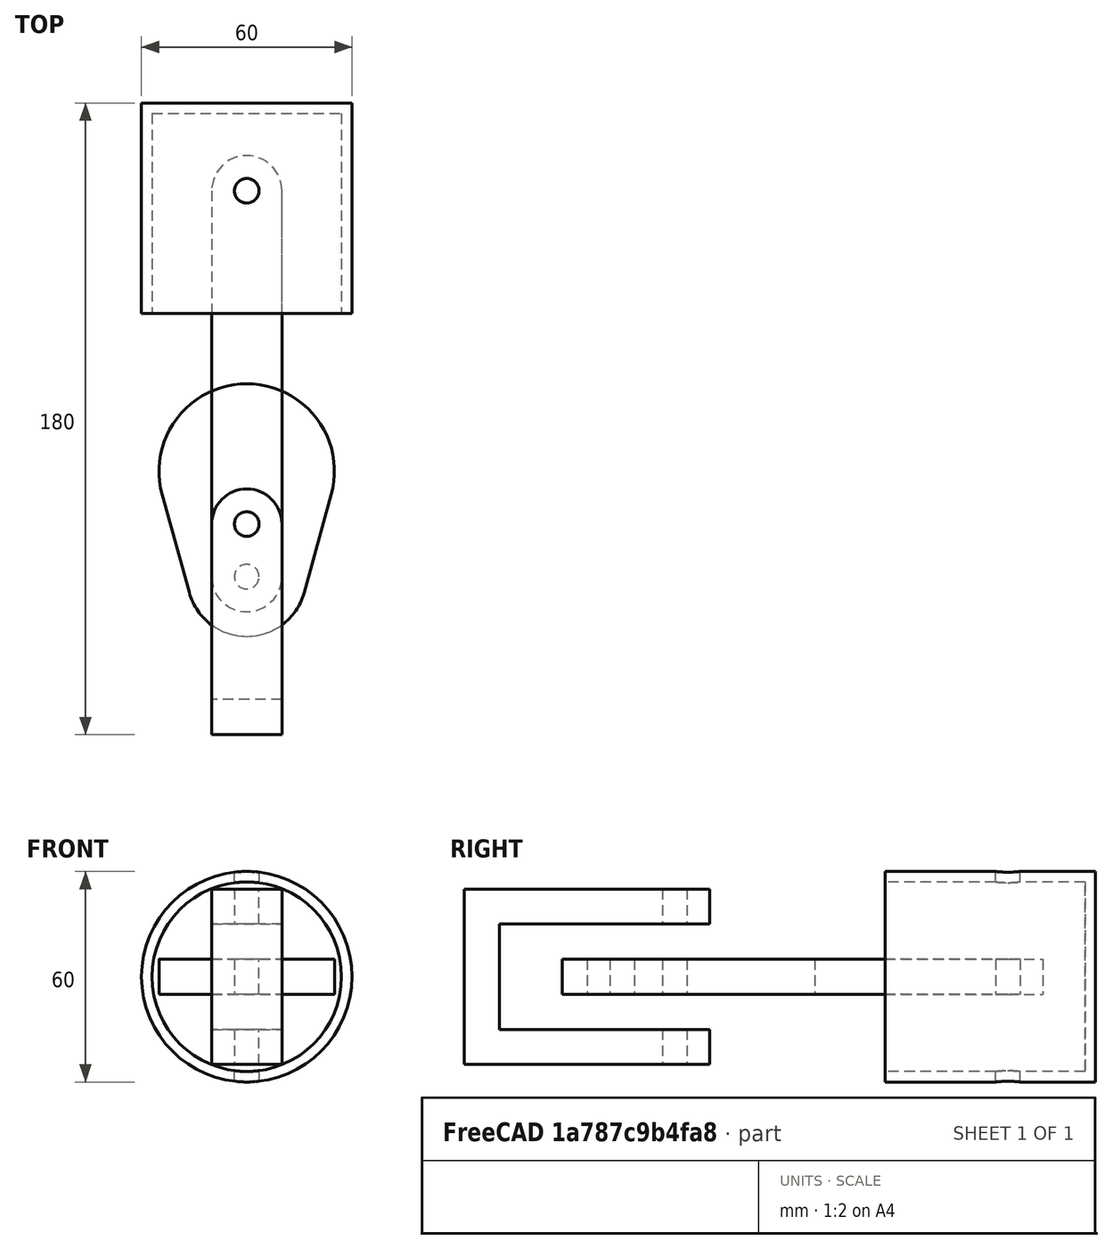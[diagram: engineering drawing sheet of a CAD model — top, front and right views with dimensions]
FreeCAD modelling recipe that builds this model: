
FCSTD DOCUMENT  (FreeCAD 1.0R39319 (Git))
Label: Piston Head Assembly
License: All rights reserved
LicenseURL: https://en.wikipedia.org/wiki/All_rights_reserved
objects: Sketcher::SketchObject×7, App::FeaturePython×6, App::Link×5, PartDesign::SubShapeBinder×4, PartDesign::Body×4, PartDesign::Pad×3, PartDesign::Pocket×2, PartDesign::Revolution×1, Assembly::JointGroup×1, Assembly::AssemblyObject×1
note: 40 computed .brp shape members not serialized (recipe doc carries the construction recipe); baked Part::Feature solids carry a one-line shape summary decoded from their .brp

FEATURE [Sketcher::SketchObject] Sketch  label="main_sketch"
  ArcFitTolerance = 1e-06
  AttachmentSupport = -> [XY_Plane]
  FullyConstrained = true
  MakeInternals = false
  MapMode = 5
  sketch-geometry (19):
    g0: ArcOfCircle CenterX=0 CenterY=55 CenterZ=0 NormalX=0 NormalY=0 NormalZ=1 AngleXU=0 Radius=10 StartAngle=3e-16 EndAngle=3.14159
    g1: ArcOfCircle CenterX=0 CenterY=-55 CenterZ=0 NormalX=0 NormalY=0 NormalZ=1 AngleXU=0 Radius=10 StartAngle=3.14159 EndAngle=6.28319
    g2: LineSegment StartX=10 StartY=55 StartZ=0 EndX=10 EndY=-55 EndZ=0
    g3: LineSegment StartX=-10 StartY=55 StartZ=0 EndX=-10 EndY=-55 EndZ=0
    g4: Circle CenterX=0 CenterY=55 CenterZ=0 NormalX=0 NormalY=0 NormalZ=1 AngleXU=0 Radius=3.5
    g5: Circle CenterX=0 CenterY=-55 CenterZ=0 NormalX=0 NormalY=0 NormalZ=1 AngleXU=0 Radius=3.5
    g6: ArcOfCircle CenterX=0 CenterY=-25 CenterZ=0 NormalX=0 NormalY=0 NormalZ=1 AngleXU=0 Radius=25 StartAngle=6.01325 EndAngle=9.69471
    g7: ArcOfCircle CenterX=0 CenterY=-55 CenterZ=0 NormalX=0 NormalY=0 NormalZ=1 AngleXU=0 Radius=17 StartAngle=3.41153 EndAngle=6.01325
    g8: LineSegment StartX=-24.0947 StartY=-31.6667 StartZ=0 EndX=-16.3844 EndY=-59.5333 EndZ=0
    g9: LineSegment StartX=16.3844 StartY=-59.5333 StartZ=0 EndX=24.0947 EndY=-31.6667 EndZ=0
    g10: Circle CenterX=8e-16 CenterY=-40 CenterZ=0 NormalX=0 NormalY=0 NormalZ=1 AngleXU=0 Radius=3.5
    g11: ArcOfCircle CenterX=8e-16 CenterY=-40 CenterZ=0 NormalX=0 NormalY=0 NormalZ=1 AngleXU=0 Radius=10 StartAngle=0 EndAngle=3.14159
    g12: LineSegment StartX=-30 StartY=80 StartZ=0 EndX=-30 EndY=20 EndZ=0
    g13: LineSegment StartX=-30 StartY=20 StartZ=0 EndX=30 EndY=20 EndZ=0
    g14: LineSegment StartX=30 StartY=20 StartZ=0 EndX=30 EndY=80 EndZ=0
    g15: LineSegment StartX=30 StartY=80 StartZ=0 EndX=-30 EndY=80 EndZ=0
    g16: LineSegment StartX=-10 StartY=-40 StartZ=0 EndX=-10 EndY=-100 EndZ=0
    g17: LineSegment StartX=10 StartY=-40 StartZ=0 EndX=10 EndY=-100 EndZ=0
    g18: LineSegment StartX=-10 StartY=-100 StartZ=0 EndX=10 EndY=-100 EndZ=0
  constraints (46):
    c: Tangent(g0,g2) = 1.5708
    c: Tangent(g0,g3) = -1.5708
    c: Tangent(g1,g2) = 1.5708
    c: Tangent(g1,g3) = -1.5708
    c: Equal(g0,g1)
    c: PointOnObject(g0,g-2)
    c: Symmetric(g0,g1,g-1)
    c: Radius(g0) = 10
    c: DistanceY(g2,g2) = 110
    c: Diameter(g4) = 7
    c: Coincident(g4,g0)
    c: Diameter(g5) = 7
    c: Coincident(g5,g1)
    c: PointOnObject(g6,g-2)
    c: DistanceY(g1,g6) = 30
    c: Radius(g6) = 25
    c: Radius(g7) = 17
    c: Coincident(g7,g1)
    c: Tangent(g8,g7) = -1.5708
    c: Tangent(g9,g7) = -1.5708
    c: Tangent(g8,g6) = -1.5708
    c: Tangent(g9,g6) = -1.5708
    c: Coincident(g11,g10)
    c: DistanceY(g10,g6) = 15
    c: Tangent(g11,g3) = -1.5708
    c: Tangent(g11,g2) = 1.5708
    c: Equal(g5,g10)
    c: Coincident(g12,g13)
    c: Coincident(g13,g14)
    c: Coincident(g14,g15)
    c: Coincident(g15,g12)
    c: Vertical(g12)
    c: Vertical(g14)
    c: Horizontal(g13)
    c: Equal(g15,g12)
    c: DistanceY(g12,g12) = 60
    c: Distance(g-1,g13) = 20
    c: Symmetric(g12,g14,g-2)
    c: Coincident(g16,g11)
    c: Vertical(g16)
    c: Coincident(g17,g11)
    c: Vertical(g17)
    c: Coincident(g18,g16)
    c: Coincident(g18,g17)
    c: Horizontal(g18)
    c: DistanceY(g16,g16) = 60
FEATURE [PartDesign::SubShapeBinder] Binder
  BindCopyOnChange = 0
  BindMode = 0
  ClaimChildren = false
  Context = -> Body [Binder.]
  Fuse = false
  MakeFace = false
  OffsetFill = false
  OffsetIntersection = false
  OffsetJoinType = 0
  OffsetOpenResult = false
  PartialLoad = false
  Refine = true
  Relative = true
  Support = -> [Sketch]
  _Version = 2
FEATURE [Sketcher::SketchObject] Sketch001
  ArcFitTolerance = 1e-06
  AttachmentSupport = -> [XY_Plane]
  ExternalGeometry = -> [Binder]
  FullyConstrained = true
  MakeInternals = false
  MapMode = 5
  sketch-geometry (6):
    g0: LineSegment StartX=-10 StartY=55 StartZ=0 EndX=-10 EndY=-55 EndZ=0
    g1: ArcOfCircle CenterX=3e-16 CenterY=-55 CenterZ=0 NormalX=0 NormalY=0 NormalZ=1 AngleXU=0 Radius=10 StartAngle=3.14159 EndAngle=6.28319
    g2: LineSegment StartX=10 StartY=-55 StartZ=0 EndX=10 EndY=55 EndZ=0
    g3: ArcOfCircle CenterX=-4e-16 CenterY=55 CenterZ=0 NormalX=0 NormalY=0 NormalZ=1 AngleXU=0 Radius=10 StartAngle=0 EndAngle=3.14159
    g4: Circle CenterX=3e-16 CenterY=-55 CenterZ=0 NormalX=0 NormalY=0 NormalZ=1 AngleXU=0 Radius=3.5
    g5: Circle CenterX=-4e-16 CenterY=55 CenterZ=0 NormalX=0 NormalY=0 NormalZ=1 AngleXU=0 Radius=3.5
  constraints (12):
    c: Coincident(g-4,g0)
    c: Coincident(g0,g-6)
    c: Tangent(g0,g1) = -1.5708
    c: Coincident(g1,g-6)
    c: Coincident(g1,g2)
    c: Coincident(g2,g-5)
    c: Tangent(g2,g3) = -1.5708
    c: Coincident(g3,g0)
    c: Coincident(g4,g1)
    c: Equal(g4,g-7)
    c: Coincident(g5,g3)
    c: Equal(g5,g-8)
FEATURE [PartDesign::SubShapeBinder] Binder001
  BindCopyOnChange = 0
  BindMode = 0
  ClaimChildren = false
  Context = -> Body001 [Binder001.]
  Fuse = false
  MakeFace = false
  OffsetFill = false
  OffsetIntersection = false
  OffsetJoinType = 0
  OffsetOpenResult = false
  PartialLoad = false
  Refine = true
  Relative = true
  Support = -> [Sketch]
  _Version = 2
FEATURE [Sketcher::SketchObject] Sketch002
  ArcFitTolerance = 1e-06
  AttachmentSupport = -> [XY_Plane001]
  ExternalGeometry = -> [Binder001]
  FullyConstrained = true
  MakeInternals = false
  MapMode = 5
  sketch-geometry (6):
    g0: LineSegment StartX=-30 StartY=20 StartZ=0 EndX=-30 EndY=80 EndZ=0
    g1: LineSegment StartX=-30 StartY=80 StartZ=0 EndX=0 EndY=80 EndZ=0
    g2: LineSegment StartX=0 StartY=80 StartZ=0 EndX=0 EndY=77 EndZ=0
    g3: LineSegment StartX=0 StartY=77 StartZ=0 EndX=-27 EndY=77 EndZ=0
    g4: LineSegment StartX=-27 StartY=77 StartZ=0 EndX=-27 EndY=20 EndZ=0
    g5: LineSegment StartX=-27 StartY=20 StartZ=0 EndX=-30 EndY=20 EndZ=0
  constraints (15):
    c: Coincident(g-6,g0)
    c: Coincident(g0,g-4)
    c: Coincident(g0,g1)
    c: Symmetric(g-4,g-4,g1)
    c: Coincident(g1,g2)
    c: PointOnObject(g2,g-2)
    c: Coincident(g2,g3)
    c: Horizontal(g3)
    c: Coincident(g3,g4)
    c: PointOnObject(g4,g-6)
    c: Vertical(g4)
    c: Coincident(g4,g5)
    c: Coincident(g5,g0)
    c: DistanceX(g5,g5) = 3
    c: DistanceY(g2,g2) = 3
FEATURE [PartDesign::Pad] Pad
  Direction = (0,0,1)
  Length = 10
  Length2 = 10
  Midplane = true
  Profile = -> Sketch001
  ReferenceAxis = -> Sketch001 [N_Axis]
  Refine = true
  Suppressed = false
  Type = 0
FEATURE [PartDesign::Body] Body  label="Link"
  AllowCompound = false
  Group = -> [Binder,Sketch001,Pad]
  Origin = -> Origin
  Tip = -> Pad
FEATURE [PartDesign::Revolution] Revolution
  Angle = 360
  Angle2 = 60
  Axis = (0,1,0)
  Base = (0,0,0)
  Profile = -> Sketch002
  ReferenceAxis = -> Sketch002 [V_Axis]
  Refine = true
  Suppressed = false
  Type = 0
FEATURE [PartDesign::SubShapeBinder] Binder002
  BindCopyOnChange = 0
  BindMode = 0
  ClaimChildren = false
  Context = -> Body002 [Binder002.]
  Fuse = false
  MakeFace = false
  OffsetFill = false
  OffsetIntersection = false
  OffsetJoinType = 0
  OffsetOpenResult = false
  PartialLoad = false
  Refine = true
  Relative = true
  Support = -> [Sketch]
  _Version = 2
FEATURE [Sketcher::SketchObject] Sketch003
  ArcFitTolerance = 1e-06
  AttachmentSupport = -> [XY_Plane002]
  ExternalGeometry = -> [Binder002]
  FullyConstrained = true
  MakeInternals = false
  MapMode = 5
  sketch-geometry (6):
    g0: LineSegment StartX=-24.0947 StartY=-31.6667 StartZ=0 EndX=-16.3844 EndY=-59.5333 EndZ=0
    g1: ArcOfCircle CenterX=0 CenterY=-55 CenterZ=0 NormalX=0 NormalY=0 NormalZ=1 AngleXU=0 Radius=17 StartAngle=3.41153 EndAngle=6.01325
    g2: LineSegment StartX=16.3844 StartY=-59.5333 StartZ=0 EndX=24.0947 EndY=-31.6667 EndZ=0
    g3: ArcOfCircle CenterX=-1.6e-15 CenterY=-25 CenterZ=0 NormalX=0 NormalY=0 NormalZ=1 AngleXU=0 Radius=25 StartAngle=6.01325 EndAngle=9.69471
    g4: Circle CenterX=0 CenterY=-40 CenterZ=0 NormalX=0 NormalY=0 NormalZ=1 AngleXU=0 Radius=3.5
    g5: Circle CenterX=0 CenterY=-55 CenterZ=0 NormalX=0 NormalY=0 NormalZ=1 AngleXU=0 Radius=3.5
  constraints (12):
    c: Coincident(g-4,g0)
    c: Tangent(g0,g1) = -1.5708
    c: Coincident(g1,g-6)
    c: Coincident(g1,g2)
    c: Coincident(g2,g-6)
    c: Tangent(g2,g3) = -1.5708
    c: Coincident(g3,g0)
    c: Coincident(g0,g-5)
    c: Coincident(g4,g-7)
    c: Equal(g4,g-7)
    c: Coincident(g5,g1)
    c: Equal(g5,g-8)
FEATURE [PartDesign::Pad] Pad001
  Direction = (0,0,1)
  Length = 10
  Length2 = 10
  Midplane = true
  Profile = -> Sketch003
  ReferenceAxis = -> Sketch003 [N_Axis]
  Refine = true
  Suppressed = false
  Type = 0
FEATURE [PartDesign::Body] Body002  label="Crank"
  AllowCompound = false
  Group = -> [Binder002,Sketch003,Pad001]
  Origin = -> Origin002
  Tip = -> Pad001
FEATURE [Sketcher::SketchObject] Sketch004
  ArcFitTolerance = 1e-06
  AttachmentSupport = -> [XY_Plane001]
  ExternalGeometry = -> [Binder001]
  FullyConstrained = true
  MakeInternals = false
  MapMode = 5
  sketch-geometry (1):
    g0: Circle CenterX=0 CenterY=55 CenterZ=0 NormalX=0 NormalY=0 NormalZ=1 AngleXU=0 Radius=3.5
  constraints (2):
    c: Coincident(g0,g-3)
    c: Equal(g0,g-3)
FEATURE [PartDesign::Pocket] Pocket
  BaseFeature = -> Revolution
  Direction = (0,0,-1)
  Length = 5
  Length2 = 5
  Midplane = true
  Profile = -> Sketch004
  ReferenceAxis = -> Sketch004 [N_Axis]
  Refine = true
  Suppressed = false
  Type = 1
FEATURE [PartDesign::Body] Body001  label="Piston Head"
  AllowCompound = false
  Group = -> [Binder001,Sketch002,Revolution,Sketch004,Pocket]
  Origin = -> Origin001
  Tip = -> Pocket
FEATURE [PartDesign::SubShapeBinder] Binder003
  BindCopyOnChange = 0
  BindMode = 0
  ClaimChildren = false
  Context = -> Body003 [Binder003.]
  Fuse = false
  MakeFace = false
  OffsetFill = false
  OffsetIntersection = false
  OffsetJoinType = 0
  OffsetOpenResult = false
  PartialLoad = false
  Refine = true
  Relative = true
  Support = -> [Sketch]
  _Version = 2
FEATURE [Sketcher::SketchObject] Sketch005
  ArcFitTolerance = 1e-06
  AttachmentSupport = -> [XY_Plane003]
  ExternalGeometry = -> [Binder003]
  FullyConstrained = true
  MakeInternals = false
  MapMode = 5
  sketch-geometry (5):
    g0: LineSegment StartX=-10 StartY=-40 StartZ=0 EndX=-10 EndY=-100 EndZ=0
    g1: LineSegment StartX=-10 StartY=-100 StartZ=0 EndX=10 EndY=-100 EndZ=0
    g2: LineSegment StartX=10 StartY=-100 StartZ=0 EndX=10 EndY=-40 EndZ=0
    g3: ArcOfCircle CenterX=1.8e-15 CenterY=-40 CenterZ=0 NormalX=0 NormalY=0 NormalZ=1 AngleXU=0 Radius=10 StartAngle=1e-16 EndAngle=3.14159
    g4: Circle CenterX=1.8e-15 CenterY=-40 CenterZ=0 NormalX=0 NormalY=0 NormalZ=1 AngleXU=0 Radius=3.5
  constraints (10):
    c: Tangent(g-4,g0) = -1.5708
    c: Coincident(g0,g1)
    c: Coincident(g1,g-6)
    c: Horizontal(g1)
    c: Coincident(g1,g2)
    c: Coincident(g2,g-5)
    c: Tangent(g2,g3) = -1.5708
    c: Coincident(g3,g0)
    c: Coincident(g4,g3)
    c: Equal(g4,g-7)
FEATURE [PartDesign::Pad] Pad002
  Direction = (0,0,1)
  Length = 50
  Length2 = 10
  Midplane = true
  Profile = -> Sketch005
  ReferenceAxis = -> Sketch005 [N_Axis]
  Refine = true
  Suppressed = false
  Type = 0
FEATURE [Sketcher::SketchObject] Sketch006
  ArcFitTolerance = 1e-06
  AttachmentSupport = -> [YZ_Plane003]
  ExternalGeometry = -> [Pad002]
  FullyConstrained = false
  MakeInternals = false
  MapMode = 5
  Placement = pos=(0,0,0) rot=(0.57735,0.57735,0.57735;2.0944rad)
  sketch-geometry (4):
    g0: LineSegment StartX=-90 StartY=15 StartZ=0 EndX=-90 EndY=-15 EndZ=0
    g1: LineSegment StartX=-90 StartY=-15 StartZ=0 EndX=-12.8642 EndY=-15 EndZ=0
    g2: LineSegment StartX=-12.8642 StartY=-15 StartZ=0 EndX=-12.8642 EndY=15 EndZ=0
    g3: LineSegment StartX=-12.8642 StartY=15 StartZ=0 EndX=-90 EndY=15 EndZ=0
  constraints (10):
    c: Coincident(g0,g1)
    c: Coincident(g1,g2)
    c: Coincident(g2,g3)
    c: Coincident(g3,g0)
    c: Vertical(g2)
    c: Horizontal(g1)
    c: Horizontal(g3)
    c: Symmetric(g0,g0,g-1)
    c: Distance(g1,g3) = 30
    c: Distance(g-3,g0) = 10
FEATURE [PartDesign::Pocket] Pocket001
  BaseFeature = -> Pad002
  Direction = (-1,0,0)
  Length = 30
  Length2 = 5
  Midplane = true
  Profile = -> Sketch006
  ReferenceAxis = -> Sketch006 [N_Axis]
  Refine = true
  Suppressed = false
  Type = 0
FEATURE [PartDesign::Body] Body003  label="Mount"
  AllowCompound = false
  Group = -> [Sketch005,Binder003,Pad002,Sketch006,Pocket001]
  Origin = -> Origin003
  Tip = -> Pocket001
FEATURE [App::Link] Mount  label="Mount001"
  LinkedObject = -> Body003
FEATURE [App::FeaturePython] GroundedJoint  # Assembly grounded joint (typed FeaturePython)
  ObjectToGround = -> Mount
FEATURE [App::Link] Crank  label="Crank001"
  LinkPlacement = pos=(9.6435,-78.8201,10) rot=(0,0,1;3.38508rad)
  LinkedObject = -> Body002
  Placement = pos=(9.6435,-78.8201,10) rot=(0,0,1;3.38508rad)
FEATURE [App::Link] Crank001  label="Crank002"
  LinkPlacement = pos=(9.6435,-78.8201,-10) rot=(0,0,1;3.38508rad)
  LinkedObject = -> Body002
  Placement = pos=(9.6435,-78.8201,-10) rot=(0,0,1;3.38508rad)
FEATURE [App::Link] Link  label="Link001"
  LinkPlacement = pos=(-1.80816,29.5278,-3e-16) rot=(0,0,-1;0.032881rad)
  LinkedObject = -> Body
  Placement = pos=(-1.80816,29.5278,-3e-16) rot=(0,0,-1;0.032881rad)
FEATURE [App::FeaturePython] Joint  label="Revolute"  # Assembly joint (typed FeaturePython)
  Activated = true
  AngleMax = 0
  AngleMin = 0
  Detach1 = false
  Detach2 = false
  Distance = 0
  Distance2 = 0
  EnableAngleMax = false
  EnableAngleMin = false
  EnableLengthMax = false
  EnableLengthMin = false
  JointType = 1 (Revolute)
  LengthMax = 0
  LengthMin = 0
  Offset2 = pos=(0,0,10) rot=(0,0,1;0rad)
  Placement1 = pos=(1.8e-15,-40,15) rot=(1,0,0;3.14159rad)
  Placement2 = pos=(1.8e-15,-40,5) rot=(0,0,1;0rad)
  Reference1 = -> Assembly [Mount.Pocket001.Edge22,Mount.Pocket001.Edge22]
  Reference2 = -> Assembly [Crank.Pad001.Edge17,Crank.Pad001.Edge17]
FEATURE [App::FeaturePython] Joint001  label="Revolute001"  # Assembly joint (typed FeaturePython)
  Activated = true
  AngleMax = 0
  AngleMin = 0
  Detach1 = false
  Detach2 = false
  Distance = 0
  Distance2 = 0
  EnableAngleMax = false
  EnableAngleMin = false
  EnableLengthMax = false
  EnableLengthMin = false
  JointType = 1 (Revolute)
  LengthMax = 0
  LengthMin = 0
  Offset2 = pos=(0,0,10) rot=(0,0,1;0rad)
  Placement1 = pos=(0,-55,-5) rot=(0,0,1;0rad)
  Placement2 = pos=(4e-16,-55,5) rot=(0,0,1;0rad)
  Reference1 = -> Assembly [Crank.Pad001.Edge14,Crank.Pad001.Edge14]
  Reference2 = -> Assembly [Link.Pad.Edge17,Link.Pad.Edge17]
FEATURE [App::FeaturePython] Joint002  label="Fixed"  # Assembly joint (typed FeaturePython)
  Activated = true
  AngleMax = 0
  AngleMin = 0
  Detach1 = false
  Detach2 = false
  Distance = 0
  Distance2 = 0
  EnableAngleMax = false
  EnableAngleMin = false
  EnableLengthMax = false
  EnableLengthMin = false
  JointType = 0 (Fixed)
  LengthMax = 0
  LengthMin = 0
  Offset2 = pos=(0,0,20) rot=(0,0,1;0rad)
  Placement1 = pos=(-5.3e-15,-33.696,-5) rot=(0,0,1;0rad)
  Placement2 = pos=(-5.3e-15,-33.696,15) rot=(0,0,1;0rad)
  Reference1 = -> Assembly [Crank.Pad001.Face7,Crank.Pad001.Face7]
  Reference2 = -> Assembly [Crank001.Pad001.Face7,Crank001.Pad001.Face7]
FEATURE [App::Link] Piston_Head  label="Piston Head001"
  LinkPlacement = pos=(7.194e-13,29.2854,0.975756) rot=(0,0.999993,0.003774;3.14159rad)
  LinkedObject = -> Body001
  Placement = pos=(7.194e-13,29.2854,0.975756) rot=(0,0.999993,0.003774;3.14159rad)
FEATURE [App::FeaturePython] Joint003  label="Revolute002"  # Assembly joint (typed FeaturePython)
  Activated = true
  AngleMax = 0
  AngleMin = 0
  Detach1 = false
  Detach2 = false
  Distance = 0
  Distance2 = 0
  EnableAngleMax = false
  EnableAngleMin = false
  EnableLengthMax = false
  EnableLengthMin = false
  JointType = 1 (Revolute)
  LengthMax = 0
  LengthMin = 0
  Offset2 = pos=(0,0,-27) rot=(0,0,1;0rad)
  Placement1 = pos=(0,55,28.3917) rot=(0,0,1;0rad)
  Placement2 = pos=(0,55,-27) rot=(0,0,1;0rad)
  Reference1 = -> Assembly [Piston_Head.Pocket.Face4,Piston_Head.Pocket.Face4]
  Reference2 = -> Assembly [Link.Pad.Face5,Link.Pad.Face5]
FEATURE [App::FeaturePython] Joint004  label="Slider"  # Assembly joint (typed FeaturePython)
  Activated = true
  AngleMax = 0
  AngleMin = 0
  Detach1 = false
  Detach2 = false
  Distance = 0
  Distance2 = 0
  EnableAngleMax = false
  EnableAngleMin = false
  EnableLengthMax = false
  EnableLengthMin = false
  JointType = 3 (Slider)
  LengthMax = 0
  LengthMin = 0
  Placement1 = pos=(-1.07e-14,80,2.9e-15) rot=(0,-0.707107,-0.707107;3.14159rad)
  Placement2 = pos=(7.265e-13,-100,0) rot=(-1,0,0;1.5708rad)
  Reference1 = -> Assembly [Piston_Head.Pocket.Face2,Piston_Head.Pocket.Face2]
  Reference2 = -> Assembly [Mount.Pocket001.Face3,Mount.Pocket001.Face3]
FEATURE [Assembly::JointGroup] Joints
  Group = -> [GroundedJoint,Joint,Joint001,Joint002,Joint003,Joint004]
FEATURE [Assembly::AssemblyObject] Assembly
  Group = -> [Joints,Mount,GroundedJoint,Crank,Crank001,Link,Joint,Joint001,Joint002,Piston_Head,Joint003,Joint004]
  Origin = -> Origin004
  Type = Assembly
